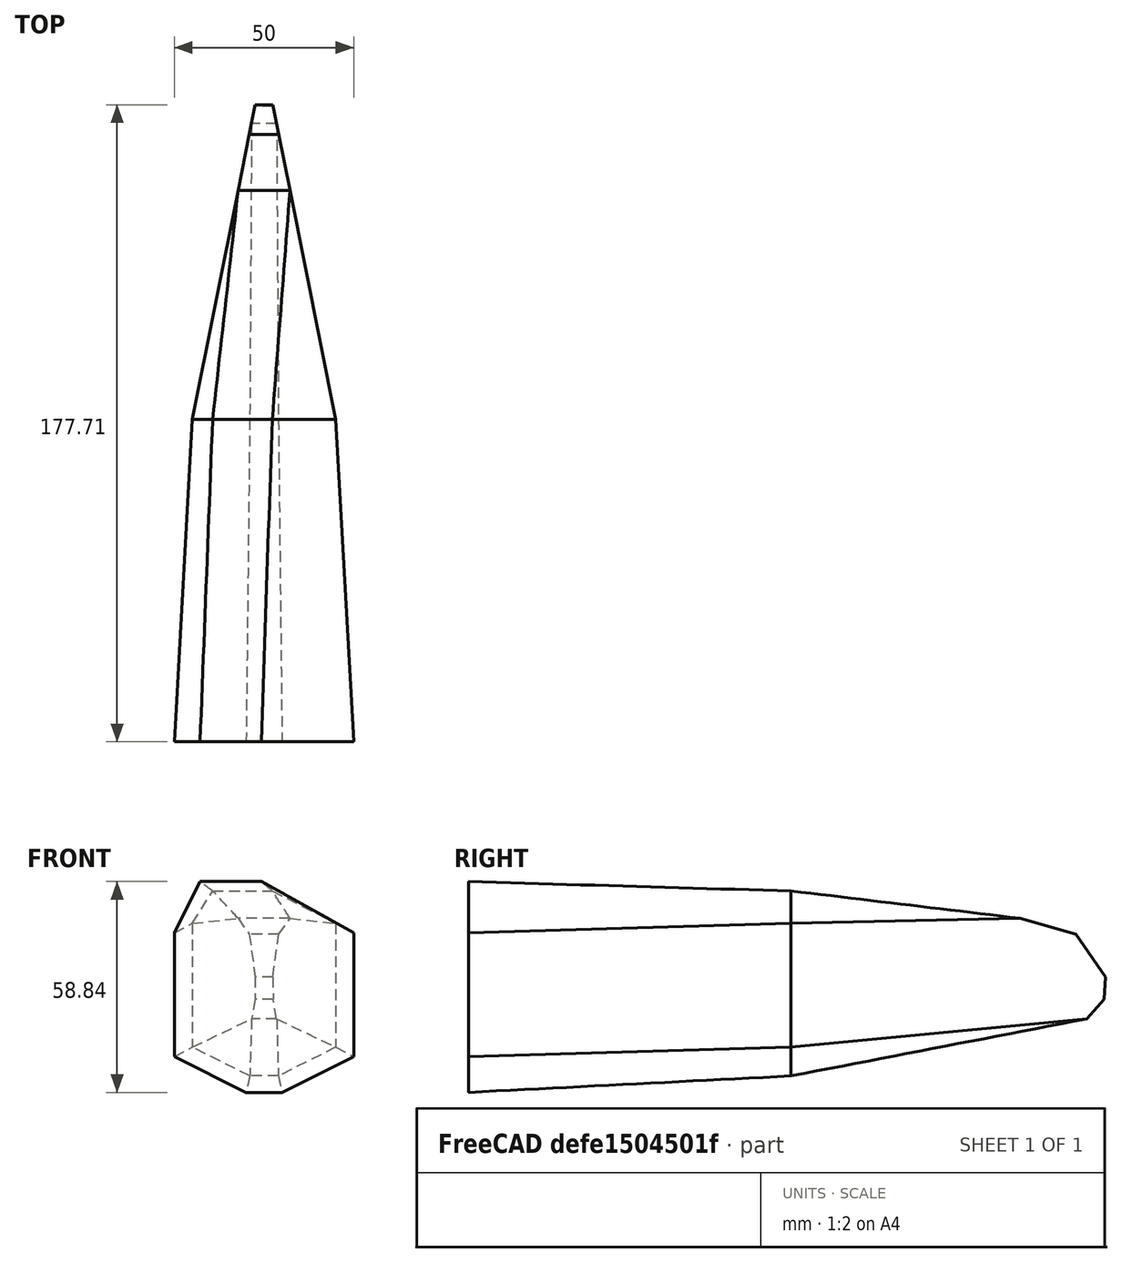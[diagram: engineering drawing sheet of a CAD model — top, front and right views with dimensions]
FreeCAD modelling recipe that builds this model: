
FCSTD DOCUMENT  (FreeCAD 0.18R4 (GitTag))
Label: o_cat_skin
License: All rights reserved
LicenseURL: http://en.wikipedia.org/wiki/All_rights_reserved
objects: Part::Feature×2, PartDesign::FeatureBase×2, PartDesign::Body×2, PartDesign::Thickness×1
note: 7 computed .brp shape members not serialized (recipe doc carries the construction recipe); baked Part::Feature solids carry a one-line shape summary decoded from their .brp

FEATURE [Part::Feature] Part__Feature  label="Pocket001"
  shape: bbox 50 x 180 x 58.84 mm, 19 faces (baked)
FEATURE [PartDesign::FeatureBase] BaseFeature
  BaseFeature = -> Part__Feature
FEATURE [PartDesign::Thickness] Thickness
  Base = -> BaseFeature [Face9]
  BaseFeature = -> BaseFeature
  Join = 0
  Mode = 0
  Value = 1
FEATURE [PartDesign::Body] Body
  BaseFeature = -> Part__Feature
  Group = -> [BaseFeature,Thickness]
  Origin = -> Origin
  Tip = -> Thickness
FEATURE [Part::Feature] Part__Feature001  label="Pocket002"
  shape: bbox 50 x 177.7 x 58.84 mm, 21 faces (baked)
FEATURE [PartDesign::FeatureBase] BaseFeature001
  BaseFeature = -> Part__Feature001
FEATURE [PartDesign::Body] Body001
  BaseFeature = -> Part__Feature001
  Group = -> [BaseFeature001]
  Origin = -> Origin001
  Tip = -> BaseFeature001
